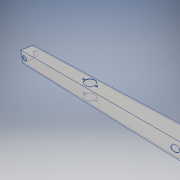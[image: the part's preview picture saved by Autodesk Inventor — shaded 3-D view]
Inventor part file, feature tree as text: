
AUTODESK INVENTOR PART (.ipt)
format: ipt  version: 2019 (Build 230136000, 136)  size: 132,608 bytes
history: native  units: in
note: dims shown in document units (in); Inventor stores cm internally (conversion verified against a paired STEP export)
features: extrude x4, sketch x4
ambient origin geometry x8: Origin, YZ Plane, XZ Plane, XY Plane, X Axis, Y Axis, Z Axis, Center Point
bodies: Solid1 (feature_tree)
feature tree (8):
  extrude  "Extrusion1"  Depth=1.5in
  extrude  "Extrusion2"  Depth=18.0in
  extrude  "Extrusion4"  Depth=15.0in TaperAngle=0.0deg
  extrude  "Extrusion5"  Depth=1.0in TaperAngle=0.0deg
  sketch  "Sketch2"  dims[d0=0.0625in d1=1.5in]
  sketch  "Sketch3"  dims[d2=18.0in d3=0.0in d4=0.5in]
  sketch  "Sketch5"  dims[d5=0.625in d6=15.0in d7=0.0in]
  sketch  "Sketch6"  dims[d11=1.125in d12=1.0in d13=0.0in d14=1.25in d15=0.25in d16=0.21in d17=1.0in d18=0.0in]
